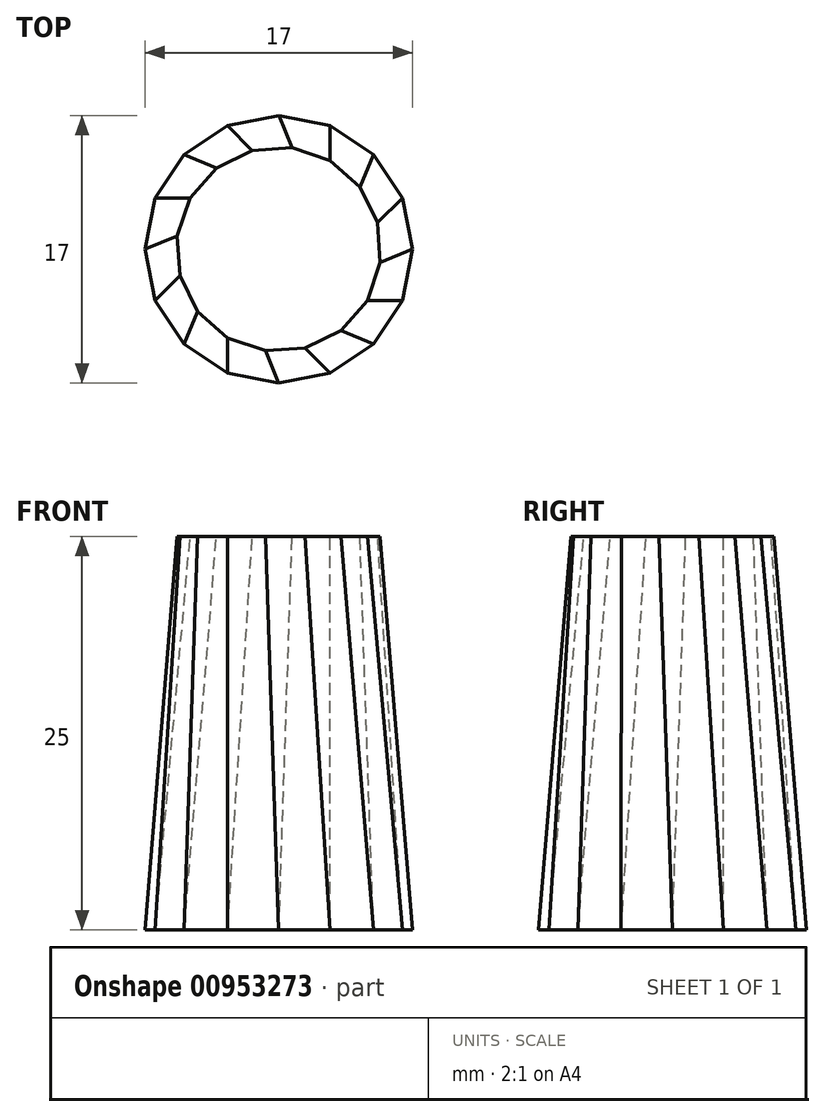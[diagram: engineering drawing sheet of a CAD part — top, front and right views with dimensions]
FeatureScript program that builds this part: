
annotation { "Feature Type Name" : "Feature", "Feature Type Description" : "" }
export const myFeature = defineFeature(function(context is Context, id is Id, definition is map)
    precondition{}
    {
        {
            var Q0;
            Q0=qCreatedBy(makeId("Top.planeOp"),FACE);
            var sketch = newSketch(context, id + "F0", { "sketchPlane" : qUnion([Q0])});
            skCircle(sketch, "E0.cCircle", {"center": v(-5.63, -3.25) * mm, "radius": 6.5 * mm, "construction": true});
            skLineSegment(sketch, "E0.0", {"start": v(0, -6.5) * mm, "end": v(-1.67, -8.4) * mm});
            skLineSegment(sketch, "E0.1", {"start": v(-1.67, -8.4) * mm, "end": v(-3.95, -9.53) * mm});
            skLineSegment(sketch, "E0.2", {"start": v(-3.95, -9.53) * mm, "end": v(-6.48, -9.7) * mm});
            skLineSegment(sketch, "E0.3", {"start": v(-6.48, -9.7) * mm, "end": v(-8.88, -8.88) * mm});
            skLineSegment(sketch, "E0.4", {"start": v(-8.88, -8.88) * mm, "end": v(-10.79, -7.2) * mm});
            skLineSegment(sketch, "E0.5", {"start": v(-10.79, -7.2) * mm, "end": v(-11.9, -4.93) * mm});
            skLineSegment(sketch, "E0.6", {"start": v(-11.9, -4.93) * mm, "end": v(-12.07, -2.4) * mm});
            skLineSegment(sketch, "E0.7", {"start": v(-12.07, -2.4) * mm, "end": v(-11.26, 0) * mm});
            skLineSegment(sketch, "E0.8", {"start": v(-11.26, 0) * mm, "end": v(-9.59, 1.9) * mm});
            skLineSegment(sketch, "E0.9", {"start": v(-9.59, 1.9) * mm, "end": v(-7.31, 3.03) * mm});
            skLineSegment(sketch, "E0.10", {"start": v(-7.31, 3.03) * mm, "end": v(-4.78, 3.2) * mm});
            skLineSegment(sketch, "E0.11", {"start": v(-4.78, 3.2) * mm, "end": v(-2.38, 2.38) * mm});
            skLineSegment(sketch, "E0.12", {"start": v(-2.38, 2.38) * mm, "end": v(-0.47, 0.7) * mm});
            skLineSegment(sketch, "E0.13", {"start": v(-0.47, 0.7) * mm, "end": v(0.65, -1.57) * mm});
            skLineSegment(sketch, "E0.14", {"start": v(0.65, -1.57) * mm, "end": v(0.82, -4.1) * mm});
            skLineSegment(sketch, "E0.15", {"start": v(0.82, -4.1) * mm, "end": v(0, -6.5) * mm});
            skSolve(sketch);
        }
        {
            var Q0;
            Q0=qCreatedBy(makeId("Top.planeOp"),FACE);
            cPlane(context, id + "F1", {"entities" : qUnion([Q0]), "cplaneType" : CPlaneType.OFFSET, "offset" : 25 * mm, "oppositeDirection" : true, "width" : 150 * mm, "height" : 150 * mm});
        }
        {
            var Q0;
            Q0=qCreatedBy(id+"F1.planeOp",FACE);
            var sketch = newSketch(context, id + "F2", { "sketchPlane" : qUnion([Q0])});
            skCircle(sketch, "E1.cCircle", {"center": v(-5.63, -3.25) * mm, "radius": 8.5 * mm, "construction": true});
            skLineSegment(sketch, "E1.0", {"start": v(2.22, 0) * mm, "end": v(2.87, -3.25) * mm});
            skLineSegment(sketch, "E1.1", {"start": v(2.87, -3.25) * mm, "end": v(2.22, -6.5) * mm});
            skLineSegment(sketch, "E1.2", {"start": v(2.22, -6.5) * mm, "end": v(0.38, -9.26) * mm});
            skLineSegment(sketch, "E1.3", {"start": v(0.38, -9.26) * mm, "end": v(-2.38, -11.1) * mm});
            skLineSegment(sketch, "E1.4", {"start": v(-2.38, -11.1) * mm, "end": v(-5.63, -11.75) * mm});
            skLineSegment(sketch, "E1.5", {"start": v(-5.63, -11.75) * mm, "end": v(-8.88, -11.1) * mm});
            skLineSegment(sketch, "E1.6", {"start": v(-8.88, -11.1) * mm, "end": v(-11.64, -9.26) * mm});
            skLineSegment(sketch, "E1.7", {"start": v(-11.64, -9.26) * mm, "end": v(-13.48, -6.5) * mm});
            skLineSegment(sketch, "E1.8", {"start": v(-13.48, -6.5) * mm, "end": v(-14.13, -3.25) * mm});
            skLineSegment(sketch, "E1.9", {"start": v(-14.13, -3.25) * mm, "end": v(-13.48, 0) * mm});
            skLineSegment(sketch, "E1.10", {"start": v(-13.48, 0) * mm, "end": v(-11.64, 2.76) * mm});
            skLineSegment(sketch, "E1.11", {"start": v(-11.64, 2.76) * mm, "end": v(-8.88, 4.6) * mm});
            skLineSegment(sketch, "E1.12", {"start": v(-8.88, 4.6) * mm, "end": v(-5.63, 5.25) * mm});
            skLineSegment(sketch, "E1.13", {"start": v(-5.63, 5.25) * mm, "end": v(-2.37, 4.6) * mm});
            skLineSegment(sketch, "E1.14", {"start": v(-2.37, 4.6) * mm, "end": v(0.38, 2.76) * mm});
            skLineSegment(sketch, "E1.15", {"start": v(0.38, 2.76) * mm, "end": v(2.22, 0) * mm});
            skSolve(sketch);
        }
        {
            var Q0;
            Q0=makeQuery(id+"F2.imprint","IMPRINT",FACE,{"disambiguationData":[TD([[makeQuery(id+"F2.imprint","IMPRINT",EDGE,{"derivedFrom":sQuery(id+"F2.wireOp",EDGE,"E1.0")}),-1.0]])]});
            var Q1;
            Q1=makeQuery(id+"F0.imprint","IMPRINT",FACE,{"disambiguationData":[TD([[makeQuery(id+"F0.imprint","IMPRINT",EDGE,{"derivedFrom":sQuery(id+"F0.wireOp",EDGE,"E0.0")}),-1.0]])]});
            loft(context, id + "F3", {"sheetProfilesArray" : [{ "sheetProfileEntities" : qUnion([Q0]) }, { "sheetProfileEntities" : qUnion([Q1]) }]});
        }
    });
